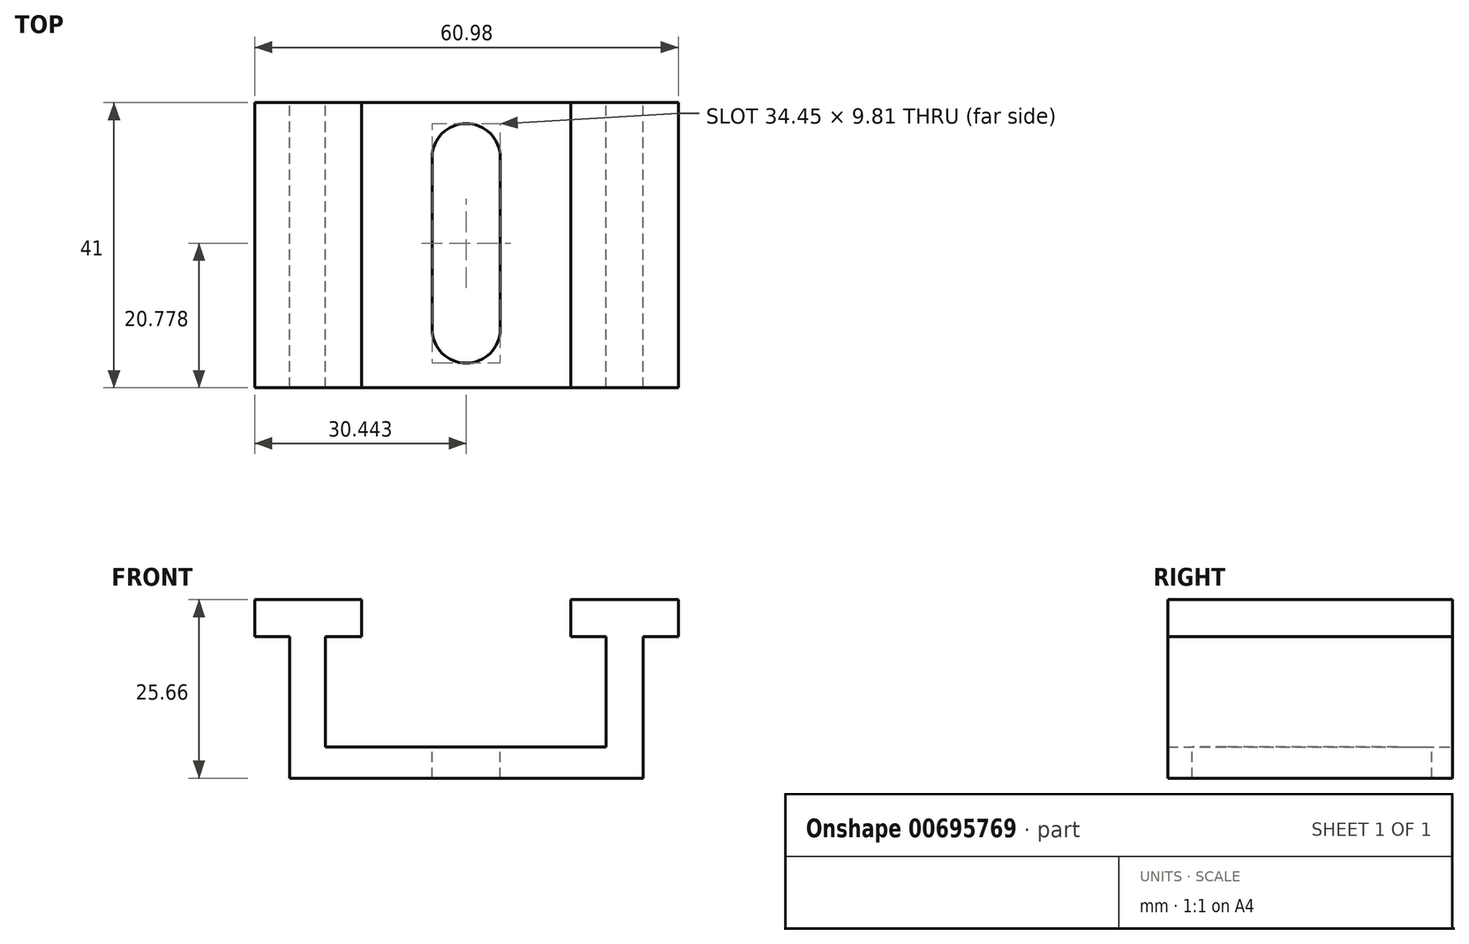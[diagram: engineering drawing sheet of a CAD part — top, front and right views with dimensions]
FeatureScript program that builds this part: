
annotation { "Feature Type Name" : "Feature", "Feature Type Description" : "" }
export const myFeature = defineFeature(function(context is Context, id is Id, definition is map)
    precondition{}
    {
        {
            var Q0;
            Q0=qCreatedBy(makeId("Front.planeOp"),FACE);
            var sketch = newSketch(context, id + "F0", { "sketchPlane" : qUnion([Q0])});
            skLineSegment(sketch, "E0", {"start": v(0, 0) * mm, "end": v(15.4, 0) * mm});
            skLineSegment(sketch, "E1", {"start": v(15.4, 0) * mm, "end": v(15.4, -5.32) * mm});
            skLineSegment(sketch, "E2", {"start": v(0, 0) * mm, "end": v(0, -5.32) * mm});
            skLineSegment(sketch, "E3", {"start": v(0, -5.32) * mm, "end": v(5.04, -5.32) * mm});
            skLineSegment(sketch, "E4", {"start": v(15.4, -5.32) * mm, "end": v(10.18, -5.32) * mm});
            skLineSegment(sketch, "E5", {"start": v(5.04, -5.32) * mm, "end": v(5.04, -25.66) * mm});
            skLineSegment(sketch, "E6", {"start": v(5.04, -25.66) * mm, "end": v(55.89, -25.66) * mm});
            skLineSegment(sketch, "E7", {"start": v(55.89, -25.66) * mm, "end": v(55.89, -5.32) * mm});
            skLineSegment(sketch, "E8", {"start": v(10.18, -5.32) * mm, "end": v(10.18, -21.19) * mm});
            skLineSegment(sketch, "E9", {"start": v(10.18, -21.19) * mm, "end": v(50.6, -21.19) * mm});
            skLineSegment(sketch, "E10", {"start": v(50.6, -21.19) * mm, "end": v(50.6, -5.32) * mm});
            skLineSegment(sketch, "E11", {"start": v(50.6, -5.32) * mm, "end": v(45.51, -5.32) * mm});
            skLineSegment(sketch, "E12", {"start": v(55.89, -5.32) * mm, "end": v(60.98, -5.32) * mm});
            skLineSegment(sketch, "E13", {"start": v(45.51, -5.32) * mm, "end": v(45.51, 0) * mm});
            skLineSegment(sketch, "E14", {"start": v(45.51, 0) * mm, "end": v(60.98, 0) * mm});
            skLineSegment(sketch, "E15", {"start": v(60.98, 0) * mm, "end": v(60.98, -5.32) * mm});
            skSolve(sketch);
        }
        {
            var Q0;
            Q0 = qSketchRegion(id + "F0", true);
            extrude(context, id + "F1", {"entities" : qUnion([Q0]), "depth" : 41 * mm, "offsetDistance" : 25 * mm});
        }
        {
            var Q0;
            Q0=makeQuery(id+"F1.opExtrude","SWEPT_FACE",FACE,{"disambiguationData":[OSD([sQuery(id+"F0.wireOp",EDGE,"E9")])]});
            var sketch = newSketch(context, id + "F2", { "sketchPlane" : qUnion([Q0])});
            skLineSegment(sketch, "E16", {"start": v(25.54, -7.9) * mm, "end": v(25.54, -32.54) * mm});
            skLineSegment(sketch, "E17", {"start": v(35.35, -7.9) * mm, "end": v(35.35, -32.54) * mm});
            skArc(sketch, "E18", {"start": v(35.35, -7.9) * mm, "mid": v(30.44, -3) * mm, "end": v(25.54, -7.9) * mm});
            skArc(sketch, "E19", {"start": v(25.54, -32.54) * mm, "mid": v(30.44, -37.45) * mm, "end": v(35.35, -32.54) * mm});
            skSolve(sketch);
        }
        {
            var Q0;
            Q0 = qSketchRegion(id + "F2", true);
            extrude(context, id + "F3", {"entities" : qUnion([Q0]), "operationType" : NewBodyOperationType.REMOVE, "oppositeDirection" : true, "depth" : 25 * mm, "offsetDistance" : 25 * mm});
        }
    });
